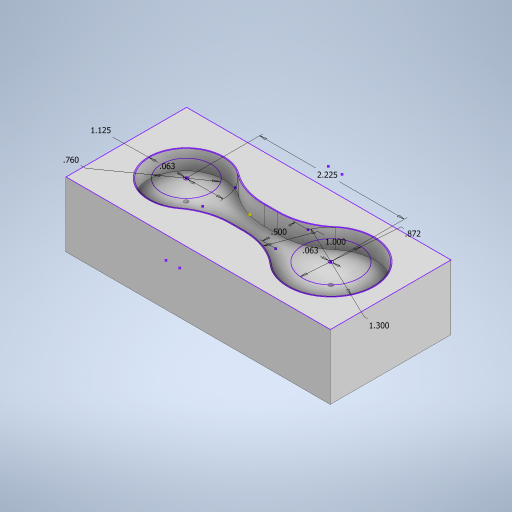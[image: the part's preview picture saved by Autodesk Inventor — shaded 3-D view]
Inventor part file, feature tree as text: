
AUTODESK INVENTOR PART (.ipt)
format: ipt  version: 2023 (Build 270158000, 158)  size: 294,912 bytes
history: native  units: in
note: dims shown in document units (in); Inventor stores cm internally (conversion verified against a paired STEP export)
features: extrude x3, sketch x1
ambient origin geometry x8: Origin, YZ Plane, XZ Plane, XY Plane, X Axis, Y Axis, Z Axis, Center Point
bodies: Body1 (feature_tree)
feature tree (4):
  sketch  "Sketch1"  dims[d15=0.872in d17=0.5in d18=1.3in d19=0.76in d20=1.125in d21=2.225in d35=1.0in d36=1.0in d37=0.0in d38=0.31in d39=0.0in d40=0.0625in d41=0.0625in d42=10.0in d43=0.0in d3=0.5in d4=0.0344in d5=0.5in d6=0.0344in d28=0.0in d29=0.0in d30=0.0in d31=0.0in]
  extrude  "Extrusion3"  Depth=0.31in
  extrude  "Extrusion4"  Depth=0.31in
  extrude  "Extrusion5"  Depth=0.31in
